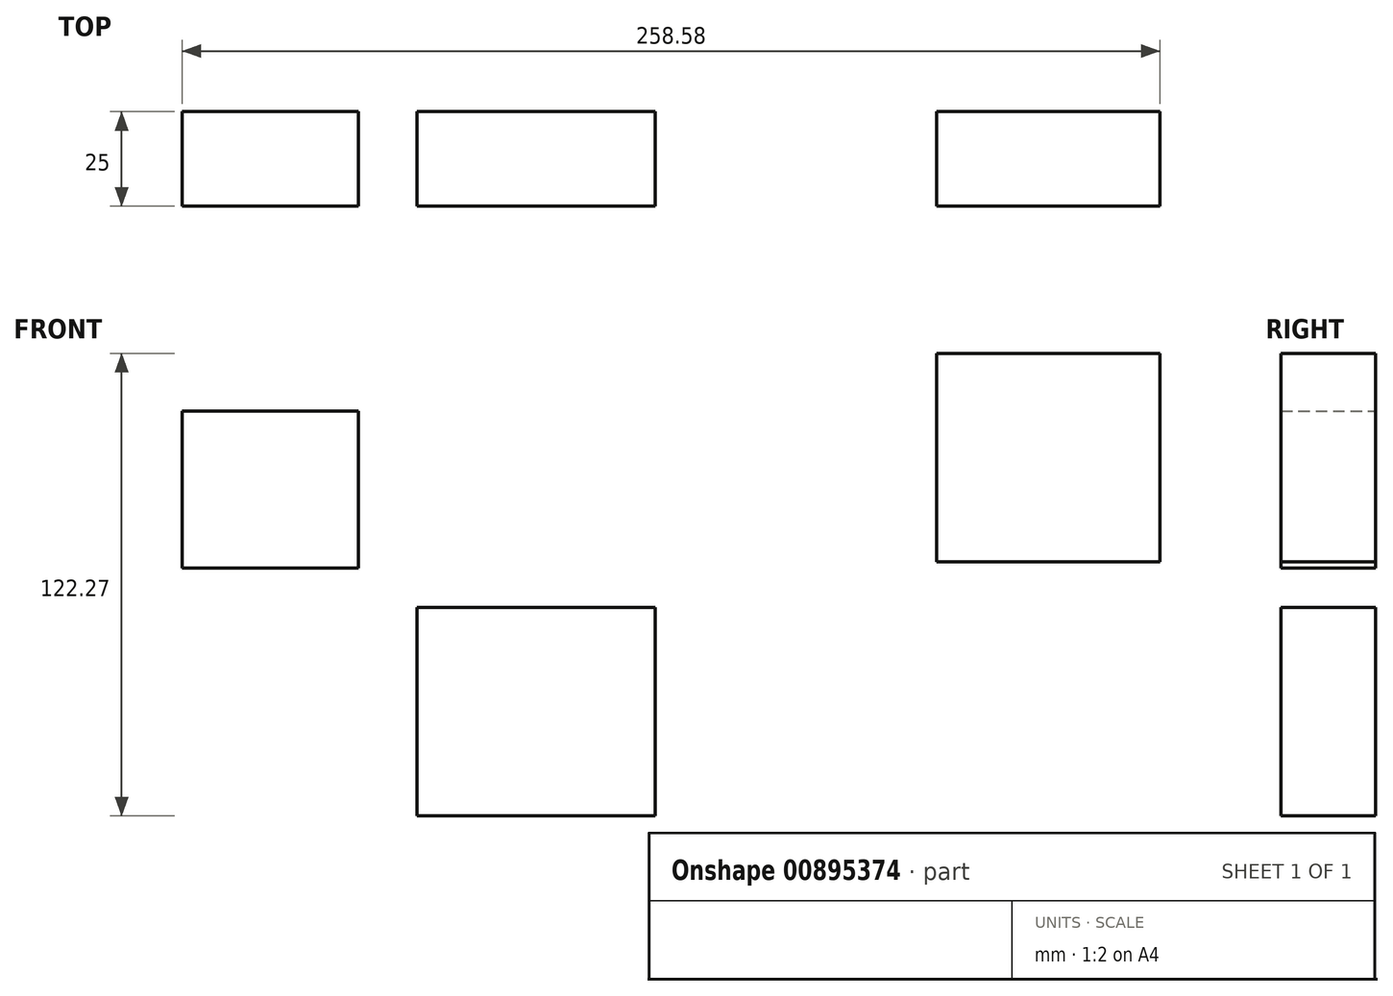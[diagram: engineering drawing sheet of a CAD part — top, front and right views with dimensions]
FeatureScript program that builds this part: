
annotation { "Feature Type Name" : "Feature", "Feature Type Description" : "" }
export const myFeature = defineFeature(function(context is Context, id is Id, definition is map)
    precondition{}
    {
        {
            var Q0;
            Q0=qCreatedBy(makeId("Front.planeOp"),FACE);
            var sketch = newSketch(context, id + "F0", { "sketchPlane" : qUnion([Q0])});
            skLineSegment(sketch, "E0.bottom", {"start": v(-116.22, 11.38) * mm, "end": v(-69.57, 11.38) * mm});
            skLineSegment(sketch, "E0.top", {"start": v(-116.22, 52.98) * mm, "end": v(-69.57, 52.98) * mm});
            skLineSegment(sketch, "E0.left", {"start": v(-116.22, 11.38) * mm, "end": v(-116.22, 52.98) * mm});
            skLineSegment(sketch, "E0.right", {"start": v(-69.57, 11.38) * mm, "end": v(-69.57, 52.98) * mm});
            skPoint(sketch, "E0.middle", {"position": v(-92.9, 32.18) * mm});
            skLineSegment(sketch, "E1.bottom", {"start": v(-54.1, -54.1) * mm, "end": v(8.85, -54.1) * mm});
            skLineSegment(sketch, "E1.top", {"start": v(-54.1, 0.98) * mm, "end": v(8.85, 0.98) * mm});
            skLineSegment(sketch, "E1.left", {"start": v(-54.1, -54.1) * mm, "end": v(-54.1, 0.98) * mm});
            skLineSegment(sketch, "E1.right", {"start": v(8.85, -54.1) * mm, "end": v(8.85, 0.98) * mm});
            skPoint(sketch, "E1.middle", {"position": v(-22.63, -26.56) * mm});
            skLineSegment(sketch, "E2.bottom", {"start": v(83.34, 13.07) * mm, "end": v(142.36, 13.07) * mm});
            skLineSegment(sketch, "E2.top", {"start": v(83.34, 68.16) * mm, "end": v(142.36, 68.16) * mm});
            skLineSegment(sketch, "E2.left", {"start": v(83.34, 13.07) * mm, "end": v(83.34, 68.16) * mm});
            skLineSegment(sketch, "E2.right", {"start": v(142.36, 13.07) * mm, "end": v(142.36, 68.16) * mm});
            skPoint(sketch, "E2.middle", {"position": v(112.85, 40.62) * mm});
            skSolve(sketch);
        }
        {
            var Q0;
            Q0 = qSketchRegion(id + "F0", true);
            extrude(context, id + "F1", {"entities" : qUnion([Q0]), "depth" : 25 * mm, "offsetDistance" : 25 * mm});
        }
    });
